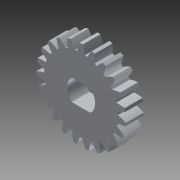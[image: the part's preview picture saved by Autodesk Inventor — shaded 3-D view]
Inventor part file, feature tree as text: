
AUTODESK INVENTOR PART (.ipt)
format: ipt  version: 2013 (Build 170138000, 138)  size: 236,032 bytes
history: native  units: mm (DEFAULTED — no unit token found)
features: plane x3, other x3, sketch x3, extrude x2
ambient origin geometry x8: Origin, YZ Plane, XZ Plane, XY Plane, X Axis, Y Axis, Z Axis, Center Point
bodies: Solid1 (feature_tree)
feature tree (11):
  extrude  "Extrusion1"  Depth=6.35mm TaperAngle=0.0deg
  plane  "Work Plane1"
  plane  "Work Plane2"
  plane  "Work Plane3"
  other  "Spur Gear"
  extrude  "Extrusion2"  Depth=76.2mm TaperAngle=0.0deg
  sketch  "Sketch1"  dims[d0=31.90875mm d1=6.35mm d2=0.0mm]
  sketch  "Sketch2"  dims[d3=29.21mm d4=76.2mm d5=0.0mm]
  other  "Srf1"
  sketch  "Sketch3"  dims[d6=0.0mm d7=1.36591mm d9=0.0mm d14=0.0mm d15=304.8mm d16=0.0mm d17=0.0mm d18=0.0mm d19=304.8mm d20=25.4mm d21=0.0mm]
  other  "Pitch Diameter"
